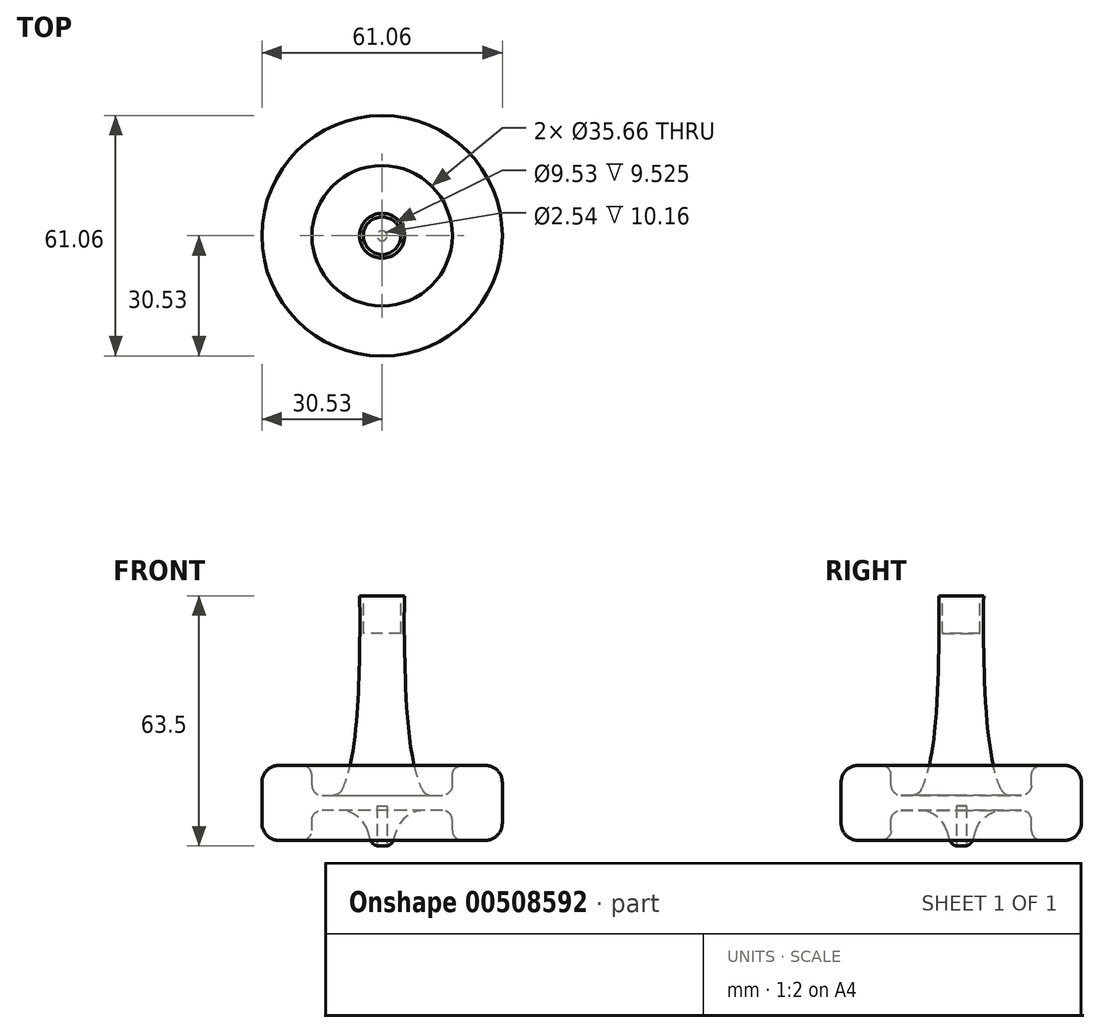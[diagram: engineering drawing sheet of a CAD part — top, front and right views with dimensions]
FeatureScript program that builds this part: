
annotation { "Feature Type Name" : "Feature", "Feature Type Description" : "" }
export const myFeature = defineFeature(function(context is Context, id is Id, definition is map)
    precondition{}
    {
        {
            var Q0;
            Q0=qCreatedBy(makeId("Front.planeOp"),FACE);
            var sketch = newSketch(context, id + "F0", { "sketchPlane" : qUnion([Q0])});
            skLineSegment(sketch, "E0", {"start": v(30.53, 20.48) * mm, "end": v(17.83, 20.48) * mm});
            skLineSegment(sketch, "E1", {"start": v(17.83, 12.86) * mm, "end": v(17.83, 20.48) * mm});
            skLineSegment(sketch, "E2", {"start": v(17.83, 12.86) * mm, "end": v(11.07, 12.86) * mm});
            skLineSegment(sketch, "E3", {"start": v(5.72, 63.5) * mm, "end": v(0, 63.5) * mm});
            skLineSegment(sketch, "E4", {"start": v(0, 63.5) * mm, "end": v(0, 0) * mm});
            skFitSpline(sketch, "E5", {"points": [v(5.72, 63.5) * mm, v(5.72, 49.88) * mm, v(11.07, 12.86) * mm], "startDerivative": vector(-1.3, -55.98) * mm, "endDerivative": vector(23.19, -30.63) * mm});
            skLineSegment(sketch, "E6", {"start": v(5.13, 9.05) * mm, "end": v(17.83, 9.05) * mm});
            skLineSegment(sketch, "E7", {"start": v(0, 0) * mm, "end": v(2.54, 0) * mm});
            skLineSegment(sketch, "E8", {"start": v(2.54, 0) * mm, "end": v(5.13, 9.05) * mm});
            skLineSegment(sketch, "E9", {"start": v(30.53, 20.48) * mm, "end": v(30.53, 1.43) * mm});
            skLineSegment(sketch, "E10", {"start": v(30.53, 1.43) * mm, "end": v(17.83, 1.43) * mm});
            skLineSegment(sketch, "E11", {"start": v(17.83, 1.43) * mm, "end": v(17.83, 9.05) * mm});
            skSolve(sketch);
        }
        {
            var Q0;
            Q0=makeQuery(id+"F0.imprint","IMPRINT",FACE,{"disambiguationData":[TD([[makeQuery(id+"F0.imprint","IMPRINT",EDGE,{"derivedFrom":sQuery(id+"F0.wireOp",EDGE,"E0")}),1.0]])]});
            var Q1;
            Q1=sQuery(id+"F0.wireOp",EDGE,"E4");
            revolve(context, id + "F1", {"entities" : qUnion([Q0]), "axis" : qUnion([Q1]), "revolveType" : RevolveType.FULL});
        }
        {
            var Q0;
            Q0=makeQuery(id+"F1.opRevolve","SWEPT_FACE",FACE,{"disambiguationData":[OSD([sQuery(id+"F0.wireOp",EDGE,"E3")])]});
            var sketch = newSketch(context, id + "F2", { "sketchPlane" : qUnion([Q0])});
            skCircle(sketch, "E12", {"center": v(0, 0) * mm, "radius": 4.76 * mm});
            skSolve(sketch);
        }
        {
            var Q0;
            Q0=makeQuery(id+"F2.imprint","IMPRINT",FACE,{"disambiguationData":[TD([[makeQuery(id+"F2.imprint","IMPRINT",EDGE,{"derivedFrom":sQuery(id+"F2.wireOp",EDGE,"E12")}),1.0]])]});
            var sketch = newSketch(context, id + "F3", { "sketchPlane" : qUnion([Q0])});
            skSolve(sketch);
        }
        {
            var Q0;
            Q0 = qSketchRegion(id + "F3", true);
            var Q1;
            Q1=makeQuery(id+"F2.imprint","IMPRINT",FACE,{"disambiguationData":[TD([[makeQuery(id+"F2.imprint","IMPRINT",EDGE,{"derivedFrom":sQuery(id+"F2.wireOp",EDGE,"E12")}),1.0]])]});
            extrude(context, id + "F4", {"entities" : qUnion([Q0, Q1]), "operationType" : NewBodyOperationType.REMOVE, "oppositeDirection" : true, "depth" : 9.52 * mm});
        }
        {
            var Q0;
            Q0=makeQuery(id+"F1.opRevolve","SWEPT_FACE",FACE,{"disambiguationData":[OSD([sQuery(id+"F0.wireOp",EDGE,"E7")])]});
            var sketch = newSketch(context, id + "F5", { "sketchPlane" : qUnion([Q0])});
            skCircle(sketch, "E13", {"center": v(0, 0) * mm, "radius": 1.27 * mm});
            skSolve(sketch);
        }
        {
            var Q0;
            Q0=makeQuery(id+"F5.imprint","IMPRINT",FACE,{"disambiguationData":[TD([[makeQuery(id+"F5.imprint","IMPRINT",EDGE,{"derivedFrom":sQuery(id+"F5.wireOp",EDGE,"E13")}),1.0]])]});
            extrude(context, id + "F6", {"entities" : qUnion([Q0]), "operationType" : NewBodyOperationType.REMOVE, "oppositeDirection" : true, "depth" : 10.16 * mm});
        }
        {
            var Q0;
            Q0=makeQuery(id+"F1.opRevolve","SWEPT_EDGE",EDGE,{"disambiguationData":[OSD([sQuery(id+"F0.wireOp",EDGE,"E7"),sQuery(id+"F0.wireOp",EDGE,"E8")])]});
            fillet(context, id + "F7", {"entities" : qUnion([Q0]), "radius" : 2.54 * mm, "tangentPropagation" : true, "allowEdgeOverflow" : false});
        }
        {
            var Q0;
            Q0=makeQuery(id+"F1.opRevolve","SWEPT_EDGE",EDGE,{"disambiguationData":[OSD([sQuery(id+"F0.wireOp",EDGE,"E6"),sQuery(id+"F0.wireOp",EDGE,"E8")])]});
            fillet(context, id + "F8", {"entities" : qUnion([Q0]), "radius" : 7.62 * mm, "tangentPropagation" : true, "allowEdgeOverflow" : false});
        }
        {
            var Q0;
            Q0=makeQuery(id+"F1.opRevolve","SWEPT_FACE",FACE,{"disambiguationData":[OSD([sQuery(id+"F0.wireOp",EDGE,"E9")])]});
            fillet(context, id + "F9", {"entities" : qUnion([Q0]), "radius" : 4.32 * mm, "tangentPropagation" : true, "allowEdgeOverflow" : false});
        }
        {
            var Q0;
            Q0=makeQuery(id+"F1.opRevolve","SWEPT_EDGE",EDGE,{"disambiguationData":[OSD([sQuery(id+"F0.wireOp",EDGE,"E2"),sQuery(id+"F0.wireOp",EDGE,"E5")])]});
            var Q1;
            Q1=makeQuery(id+"F1.opRevolve","SWEPT_EDGE",EDGE,{"disambiguationData":[OSD([sQuery(id+"F0.wireOp",EDGE,"E1"),sQuery(id+"F0.wireOp",EDGE,"E2")])]});
            var Q2;
            Q2=makeQuery(id+"F1.opRevolve","SWEPT_FACE",FACE,{"disambiguationData":[OSD([sQuery(id+"F0.wireOp",EDGE,"E1")])]});
            fillet(context, id + "F10", {"entities" : qUnion([Q0, Q1, Q2]), "radius" : 2.54 * mm, "tangentPropagation" : true, "allowEdgeOverflow" : false});
        }
        {
            var Q0;
            Q0=makeQuery(id+"F1.opRevolve","SWEPT_FACE",FACE,{"disambiguationData":[OSD([sQuery(id+"F0.wireOp",EDGE,"E11")])]});
            fillet(context, id + "F11", {"entities" : qUnion([Q0]), "radius" : 2.54 * mm, "tangentPropagation" : true, "allowEdgeOverflow" : false});
        }
    });
